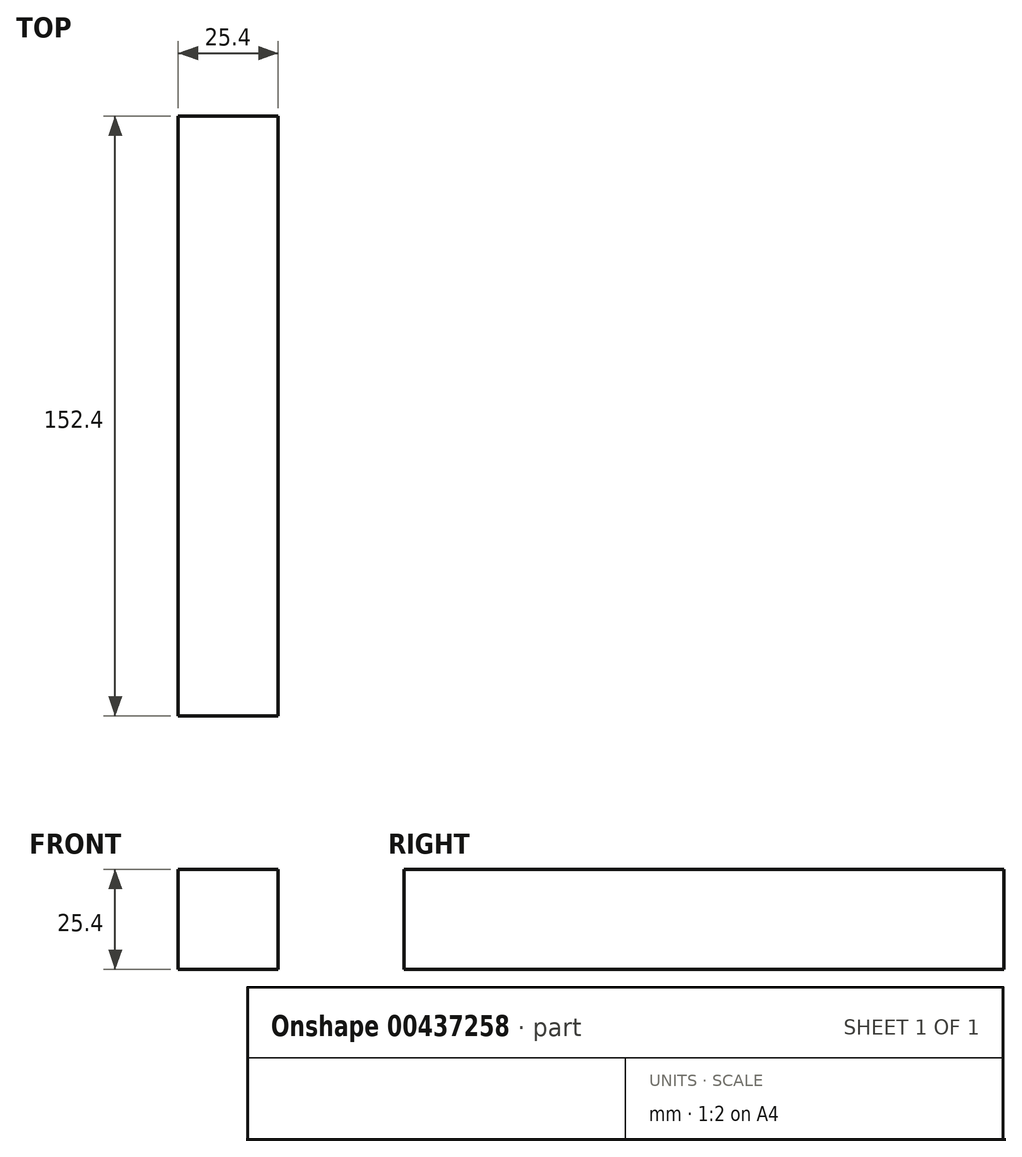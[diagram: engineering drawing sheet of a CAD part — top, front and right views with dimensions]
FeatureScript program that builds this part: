
annotation { "Feature Type Name" : "Feature", "Feature Type Description" : "" }
export const myFeature = defineFeature(function(context is Context, id is Id, definition is map)
    precondition{}
    {
        {
            var Q0;
            Q0=qCreatedBy(makeId("Front.planeOp"),FACE);
            var sketch = newSketch(context, id + "F0", { "sketchPlane" : qUnion([Q0])});
            skLineSegment(sketch, "E0.bottom", {"start": v(-12.7, 12.7) * mm, "end": v(12.7, 12.7) * mm});
            skLineSegment(sketch, "E0.top", {"start": v(-12.7, -12.7) * mm, "end": v(12.7, -12.7) * mm});
            skLineSegment(sketch, "E0.left", {"start": v(-12.7, 12.7) * mm, "end": v(-12.7, -12.7) * mm});
            skLineSegment(sketch, "E0.right", {"start": v(12.7, 12.7) * mm, "end": v(12.7, -12.7) * mm});
            skPoint(sketch, "E0.middle", {"position": v(0, 0) * mm});
            skSolve(sketch);
        }
        {
            var Q0;
            Q0=makeQuery(id+"F0.imprint","IMPRINT",FACE,{"disambiguationData":[TD([[makeQuery(id+"F0.imprint","IMPRINT",EDGE,{"derivedFrom":sQuery(id+"F0.wireOp",EDGE,"E0.bottom")}),-1.0]])]});
            extrude(context, id + "F1", {"entities" : qUnion([Q0]), "depth" : 152.4 * mm});
        }
    });
